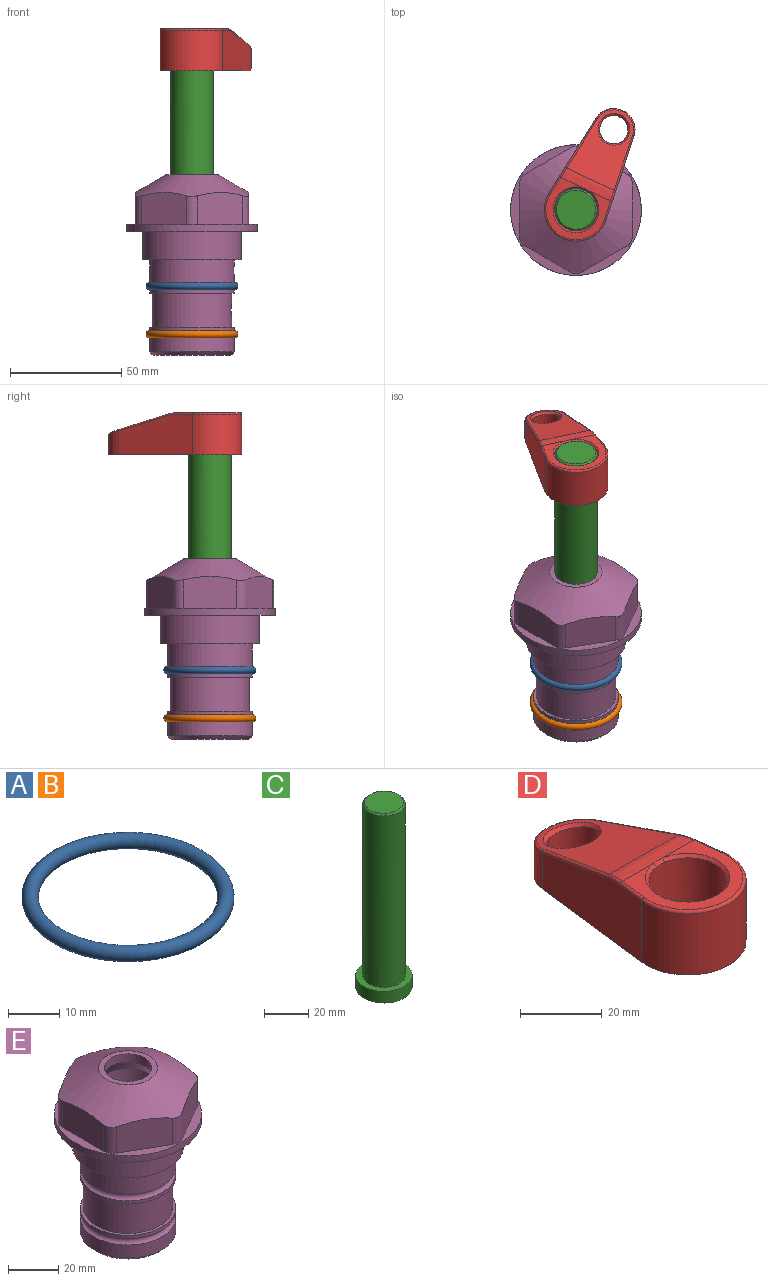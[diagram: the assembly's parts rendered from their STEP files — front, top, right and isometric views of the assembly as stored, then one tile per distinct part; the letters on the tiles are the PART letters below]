
ASSEMBLY  parts=5 mates=4
PART A: 1 faces, bbox 44.7x44.7x3.2 mm
  f0: torus R=19.05mm, axis (0,0,1), area 1193.9mm2
PART B: same geometry as A
PART C: 6 faces, bbox 25.4x25.4x101.6 mm
  f0: plane 17.46x17.46mm, normal (0,0,1), area 239.5mm2, adj f5
  f1: plane 25.4x25.4mm, normal (0,0,-1), area 506.7mm2, adj f2
  f2: cylinder r=12.7mm len=25.4mm, axis (0,0,1), area 506.7mm2, adj f1,f3
  f3: plane 25.4x25.4mm, normal (0,0,1), area 221.7mm2, adj f2,f4
  f4: cylinder r=9.53mm len=94.46mm, axis (0,0,1), area 5653mm2, adj f3,f5
  f5: cone r=8.73mm half-angle=45deg, axis (0,0,-1), area 64.4mm2, adj f0,f4
PART D: 31 faces, bbox 31.7x65.5x19.8 mm
  f0: plane 39.12x18.26mm, normal (0.99,0.12,0), area 612.2mm2, adj f1,f4,f7,f11,f13,f15
  f1: cylinder r=9.53mm len=18.91mm, axis (0,0,-1), area 296.1mm2, adj f0,f2,f7,f17
  f2: plane 39.12x18.26mm, normal (-0.99,0.12,0), area 612.2mm2, adj f1,f4,f7,f12,f14,f16
  f3: cylinder r=6.35mm len=12.7mm, axis (0,0,-1), area 362.4mm2, adj f7,f18
  f4: cylinder r=14.29mm len=28.58mm, axis (0,0,-1), area 882.2mm2, adj f0,f2,f7,f10
  f5: cylinder r=9.53mm len=19.05mm, axis (0,0,-1), area 1092.6mm2, adj f7,f19,f20
  f6: plane 26.99x23.69mm, normal (0,0,1), area 216.2mm2, adj f9,f10,f11,f12,f19
  f7: plane 63.5x28.58mm, normal (0,0,-1), area 661.8mm2, adj f0,f1,f2,f3,f4,f5,f22,f23
  f8: plane 33.52x23.6mm, normal (0,0.26,0.97), area 486mm2, adj f9,f15,f16,f17,f18
  f9: cylinder r=19.05mm len=24.72mm, axis (1,0,0), area 120.4mm2, adj f6,f8,f13,f14,f20
  f10: torus R=13.49mm, axis (0,0,1), area 59mm2, adj f4,f6,f11,f12
  f11: cylinder r=0.79mm len=8.67mm, axis (0.12,-0.99,0), area 10.8mm2, adj f0,f6,f10,f13
  f12: cylinder r=0.79mm len=8.67mm, axis (0.12,0.99,0), area 10.8mm2, adj f2,f6,f10,f14
  f13: bspline ~4.95x1.42mm, area 6.1mm2, adj f0,f9,f11,f15
  f14: bspline ~4.95x1.42mm, area 6.1mm2, adj f2,f9,f12,f16
  f15: cylinder r=0.79mm len=25.95mm, axis (0.12,-0.96,0.26), area 32.9mm2, adj f0,f8,f13,f17
  f16: cylinder r=0.79mm len=25.95mm, axis (0.12,0.96,-0.26), area 32.9mm2, adj f2,f8,f14,f17
  f17: bspline ~18.91x8.38mm, area 30mm2, adj f1,f8,f15,f16
  f18: bspline ~14.29x14.29mm, area 48.3mm2, adj f3,f8
  f19: cone r=9.53mm half-angle=45deg, axis (0,0,1), area 66.5mm2, adj f5,f6,f20
  f20: bspline ~3.22x0.96mm, area 3.5mm2, adj f5,f9,f19
  f21: plane 2.75x2.72mm, normal (0,0,-1), area 2.9mm2, adj f23,f25,f28
  f22: plane 23.05x15.88mm, normal (-0.99,-0.12,0), area 323.6mm2, adj f7,f25,f26,f27,f28,f29
  f23: plane 23.05x15.88mm, normal (0.99,-0.12,0), area 323.6mm2, adj f7,f21,f25,f27,f28,f30
  f24: cylinder r=9.53mm len=10.69mm, axis (0,0,-1), area 114.7mm2, adj f7,f27,f29,f30
  f25: cylinder r=12.7mm len=20.59mm, axis (0,0,-1), area 381.1mm2, adj f7,f21,f22,f23,f26,f28
  f26: plane 2.75x2.72mm, normal (0,0,-1), area 2.9mm2, adj f22,f25,f28
  f27: plane 19.72x18.37mm, normal (0,-0.26,-0.97), area 291.8mm2, adj f22,f23,f24,f28,f29,f30
  f28: cylinder r=15.88mm len=19.92mm, axis (1,0,0), area 54.8mm2, adj f21,f22,f23,f25,f26,f27
  f29: cylinder r=1.59mm len=11mm, axis (0,0,-1), area 34.7mm2, adj f7,f22,f24,f27
  f30: cylinder r=1.59mm len=11mm, axis (0,0,-1), area 34.7mm2, adj f7,f23,f24,f27
PART E: 36 faces, bbox 58.7x58.7x81 mm
  f0: cylinder r=17.78mm len=35.56mm, axis (0,0,1), area 1670.8mm2, adj f23,f24,f31
  f1: cylinder r=19.05mm len=38.1mm, axis (0,0,1), area 1191.9mm2, adj f26,f27,f30
  f2: plane 58.66x58.66mm, normal (0,0,-1), area 1150.6mm2, adj f3,f28
  f3: cylinder r=29.33mm len=58.66mm, axis (0,0,-1), area 585.1mm2, adj f2,f4
  f4: plane 58.66x58.66mm, normal (0,0,1), area 475.9mm2, adj f3,f5,f6,f7,f8,f9,f10,f11
  f5: plane 20.32x14.34mm, normal (-0.5,0.87,0), area 324.4mm2, adj f4,f15,f16,f17
  f6: plane 20.32x14.34mm, normal (0.5,0.87,0), area 324.4mm2, adj f4,f14,f15,f17
  f7: plane 23.48x14.34mm, normal (1,0,0), area 324.4mm2, adj f4,f13,f14,f17
  f8: plane 20.32x14.34mm, normal (0.5,-0.87,0), area 324.4mm2, adj f4,f12,f13,f17
  f9: plane 20.32x14.34mm, normal (-0.5,-0.87,0), area 324.4mm2, adj f4,f11,f12,f17
  f10: plane 23.48x14.34mm, normal (-1,0,0), area 324.4mm2, adj f4,f11,f16,f17
  f11: cylinder r=5.08mm len=12.85mm, axis (0,0,-1), area 67.2mm2, adj f4,f9,f10,f17
  f12: cylinder r=5.08mm len=12.85mm, axis (0,0,-1), area 67.2mm2, adj f4,f8,f9,f17
  f13: cylinder r=5.08mm len=12.85mm, axis (0,0,-1), area 67.2mm2, adj f4,f7,f8,f17
  f14: cylinder r=5.08mm len=12.85mm, axis (0,0,-1), area 67.2mm2, adj f4,f6,f7,f17
  f15: cylinder r=5.08mm len=12.85mm, axis (0,0,-1), area 67.2mm2, adj f4,f5,f6,f17
  f16: cylinder r=5.08mm len=12.85mm, axis (0,0,-1), area 67.2mm2, adj f4,f5,f10,f17
  f17: cone r=11.73mm half-angle=60deg, axis (0,0,-1), area 2071.8mm2, adj f5,f6,f7,f8,f9,f10,f11,f12
  f18: plane 23.46x23.46mm, normal (0,0,1), area 147.4mm2, adj f17,f35
  f19: plane 34.93x34.93mm, normal (0,0,-1), area 958mm2, adj f29
  f20: cylinder r=19.05mm len=38.1mm, axis (0,0,1), area 760.1mm2, adj f21,f29
  f21: torus R=19.05mm, axis (0,0,1), area 565.3mm2, adj f20,f22
  f22: cylinder r=19.05mm len=38.1mm, axis (0,0,1), area 190mm2, adj f21,f23
  f23: plane 38.1x38.1mm, normal (0,0,1), area 146.9mm2, adj f0,f22
  f24: plane 38.1x38.1mm, normal (0,0,-1), area 146.9mm2, adj f0,f25
  f25: cylinder r=19.05mm len=38.1mm, axis (0,0,1), area 190mm2, adj f24,f26
  f26: torus R=19.05mm, axis (0,0,1), area 565.3mm2, adj f1,f25
  f27: plane 44.45x44.45mm, normal (0,0,-1), area 411.7mm2, adj f1,f28
  f28: cylinder r=22.23mm len=44.45mm, axis (0,0,1), area 1773.5mm2, adj f2,f27
  f29: cone r=19.05mm half-angle=45deg, axis (0,0,1), area 257.5mm2, adj f19,f20
  f30: cylinder r=3.17mm len=6.75mm, axis (-1,0,0), area 128mm2, adj f1,f33
  f31: cylinder r=3.17mm len=6.35mm, axis (-1,0,0), area 102.5mm2, adj f0,f33
  f32: plane 25.4x25.4mm, normal (0,0,1), area 506.7mm2, adj f33
  f33: cylinder r=12.7mm len=66.42mm, axis (0,0,-1), area 5236.2mm2, adj f30,f31,f32,f34
  f34: cone r=9.53mm half-angle=30deg, axis (0,0,-1), area 443.4mm2, adj f33,f35
  f35: cylinder r=9.53mm len=19.05mm, axis (0,0,-1), area 240.9mm2, adj f18,f34
PLACE A at identity
PLACE B t=(0,0,-21.59)mm
PLACE C rot(axis=(0,0,-1),25.3deg) t=(0,0,27.55)mm
PLACE D rot(axis=(0,0,-1),25.3deg) t=(0,0,27.55)mm
PLACE E at identity fixed
MATE cylindrical C.f2 <-> E.f0  axis (0,0,-1) through (0,0,-10.55)mm
MATE fastened A.f0 <-> E.f0  axis (0,0,1) through (0,0,-24.51)mm
MATE fastened D.f4 <-> C.f2  axis (0,0,1) through (0,0,91.05)mm
MATE fastened B.f0 <-> E.f0  axis (0,0,1) through (0,0,-46.1)mm
